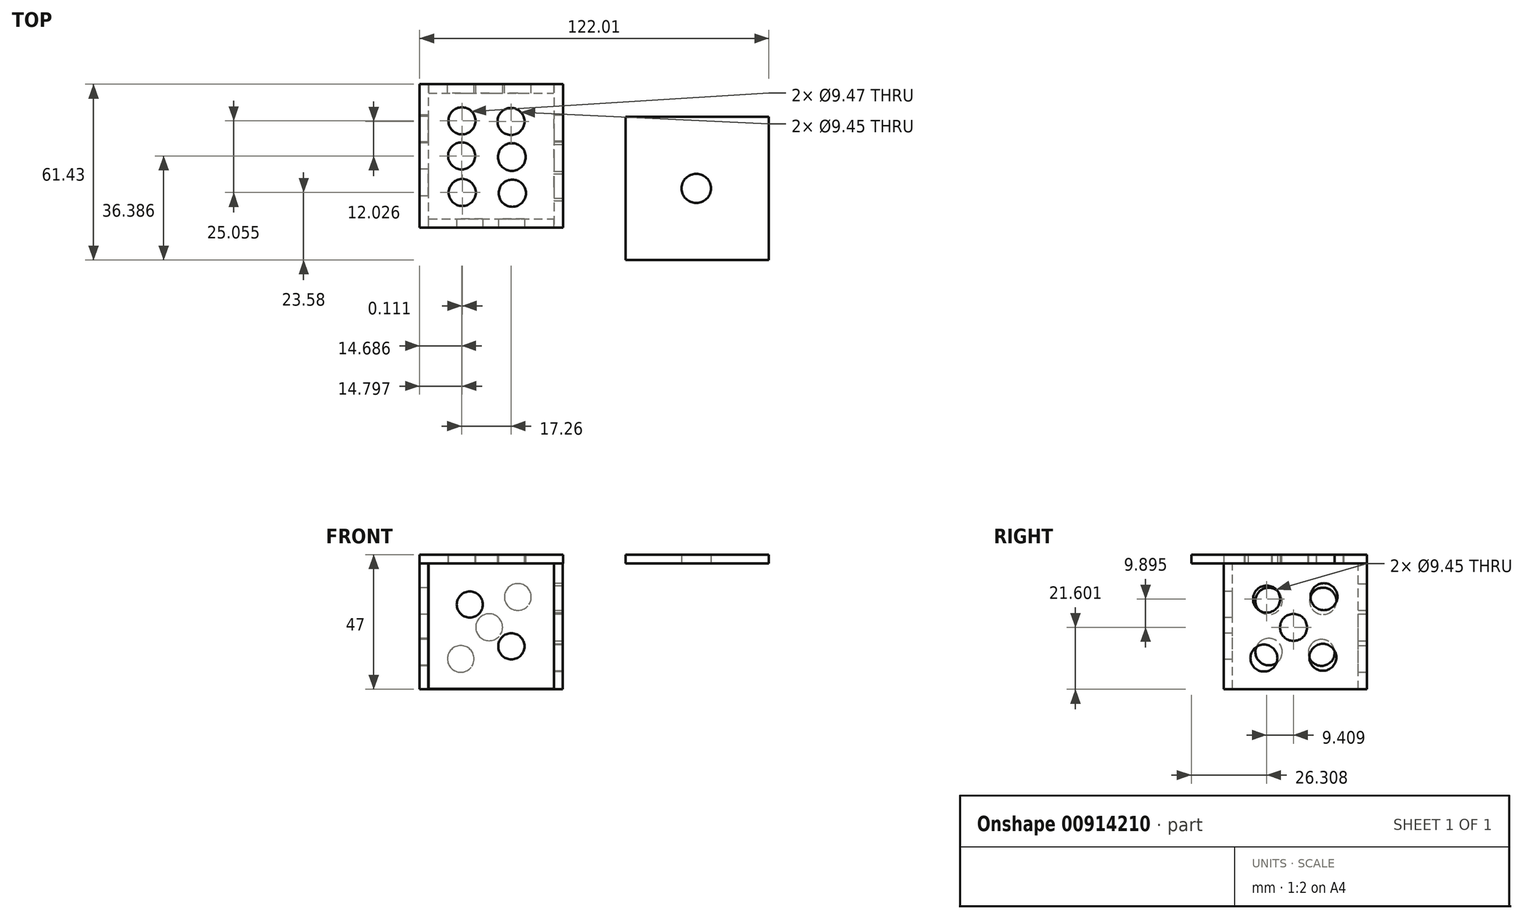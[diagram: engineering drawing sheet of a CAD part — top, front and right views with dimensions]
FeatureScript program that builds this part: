
annotation { "Feature Type Name" : "Feature", "Feature Type Description" : "" }
export const myFeature = defineFeature(function(context is Context, id is Id, definition is map)
    precondition{}
    {
        {
            var Q0;
            Q0=qCreatedBy(makeId("Top.planeOp"),FACE);
            var sketch = newSketch(context, id + "F0", { "sketchPlane" : qUnion([Q0])});
            skLineSegment(sketch, "E0.bottom", {"start": v(-67.18, 63.94) * mm, "end": v(-17.07, 63.94) * mm});
            skLineSegment(sketch, "E0.top", {"start": v(-67.18, 13.83) * mm, "end": v(-17.07, 13.83) * mm});
            skLineSegment(sketch, "E0.left", {"start": v(-67.18, 63.94) * mm, "end": v(-67.18, 13.83) * mm});
            skLineSegment(sketch, "E0.right", {"start": v(-17.07, 63.94) * mm, "end": v(-17.07, 13.83) * mm});
            skSolve(sketch);
        }
        {
            var Q0;
            Q0 = qSketchRegion(id + "F0", true);
            extrude(context, id + "F1", {"entities" : qUnion([Q0]), "depth" : 3 * mm, "offsetDistance" : 25 * mm});
        }
        {
            var Q0;
            Q0=qCreatedBy(makeId("Top.planeOp"),FACE);
            var sketch = newSketch(context, id + "F2", { "sketchPlane" : qUnion([Q0])});
            skLineSegment(sketch, "E1.bottom", {"start": v(-17.24, 63.94) * mm, "end": v(-20.28, 63.94) * mm});
            skLineSegment(sketch, "E1.top", {"start": v(-17.24, 13.82) * mm, "end": v(-20.28, 13.82) * mm});
            skLineSegment(sketch, "E1.left", {"start": v(-17.24, 63.94) * mm, "end": v(-17.24, 13.82) * mm});
            skLineSegment(sketch, "E1.right", {"start": v(-20.28, 63.94) * mm, "end": v(-20.28, 13.82) * mm});
            skSolve(sketch);
        }
        {
            var Q0;
            Q0 = qSketchRegion(id + "F2", true);
            extrude(context, id + "F3", {"entities" : qUnion([Q0]), "operationType" : NewBodyOperationType.ADD, "oppositeDirection" : true, "depth" : 44 * mm, "offsetDistance" : 25 * mm});
        }
        {
            var Q0;
            Q0=qCreatedBy(makeId("Top.planeOp"),FACE);
            var sketch = newSketch(context, id + "F4", { "sketchPlane" : qUnion([Q0])});
            skLineSegment(sketch, "E2.bottom", {"start": v(-67.2, 63.94) * mm, "end": v(-64.15, 63.94) * mm});
            skLineSegment(sketch, "E2.top", {"start": v(-67.2, 13.89) * mm, "end": v(-64.15, 13.89) * mm});
            skLineSegment(sketch, "E2.left", {"start": v(-67.2, 63.94) * mm, "end": v(-67.2, 13.89) * mm});
            skLineSegment(sketch, "E2.right", {"start": v(-64.15, 63.94) * mm, "end": v(-64.15, 13.89) * mm});
            skSolve(sketch);
        }
        {
            var Q0;
            Q0 = qSketchRegion(id + "F4", true);
            extrude(context, id + "F5", {"entities" : qUnion([Q0]), "operationType" : NewBodyOperationType.ADD, "oppositeDirection" : true, "depth" : 44 * mm, "offsetDistance" : 25 * mm});
        }
        {
            var Q0;
            Q0=qCreatedBy(makeId("Top.planeOp"),FACE);
            var sketch = newSketch(context, id + "F6", { "sketchPlane" : qUnion([Q0])});
            skLineSegment(sketch, "E3.bottom", {"start": v(-64.05, 13.88) * mm, "end": v(-20.01, 13.88) * mm});
            skLineSegment(sketch, "E3.top", {"start": v(-64.05, 16.88) * mm, "end": v(-20.01, 16.88) * mm});
            skLineSegment(sketch, "E3.left", {"start": v(-64.05, 13.88) * mm, "end": v(-64.05, 16.88) * mm});
            skLineSegment(sketch, "E3.right", {"start": v(-20.01, 13.88) * mm, "end": v(-20.01, 16.88) * mm});
            skSolve(sketch);
        }
        {
            var Q0;
            Q0 = qSketchRegion(id + "F6", true);
            extrude(context, id + "F7", {"entities" : qUnion([Q0]), "operationType" : NewBodyOperationType.ADD, "oppositeDirection" : true, "depth" : 43.8 * mm, "offsetDistance" : 25 * mm});
        }
        {
            var Q0;
            Q0=qCreatedBy(makeId("Top.planeOp"),FACE);
            var sketch = newSketch(context, id + "F8", { "sketchPlane" : qUnion([Q0])});
            skLineSegment(sketch, "E4.bottom", {"start": v(-64.1, 63.88) * mm, "end": v(-20.32, 63.88) * mm});
            skLineSegment(sketch, "E4.top", {"start": v(-64.1, 60.83) * mm, "end": v(-20.32, 60.83) * mm});
            skLineSegment(sketch, "E4.left", {"start": v(-64.1, 63.88) * mm, "end": v(-64.1, 60.83) * mm});
            skLineSegment(sketch, "E4.right", {"start": v(-20.32, 63.88) * mm, "end": v(-20.32, 60.83) * mm});
            skSolve(sketch);
        }
        {
            var Q0;
            Q0 = qSketchRegion(id + "F8", true);
            extrude(context, id + "F9", {"entities" : qUnion([Q0]), "operationType" : NewBodyOperationType.ADD, "oppositeDirection" : true, "depth" : 44 * mm, "offsetDistance" : 25 * mm});
        }
        {
            var Q0;
            Q0=qCreatedBy(makeId("Top.planeOp"),FACE);
            var sketch = newSketch(context, id + "F10", { "sketchPlane" : qUnion([Q0])});
            skLineSegment(sketch, "E5.bottom", {"start": v(4.73, 2.51) * mm, "end": v(54.81, 2.51) * mm});
            skLineSegment(sketch, "E5.top", {"start": v(4.73, 52.6) * mm, "end": v(54.81, 52.6) * mm});
            skLineSegment(sketch, "E5.left", {"start": v(4.73, 2.51) * mm, "end": v(4.73, 52.6) * mm});
            skLineSegment(sketch, "E5.right", {"start": v(54.81, 2.51) * mm, "end": v(54.81, 52.6) * mm});
            skSolve(sketch);
        }
        {
            var Q0;
            Q0 = qSketchRegion(id + "F10", true);
            extrude(context, id + "F11", {"entities" : qUnion([Q0]), "depth" : 3 * mm, "offsetDistance" : 25 * mm});
        }
        {
            var Q0;
            Q0=makeQuery(id+"F11.opExtrude","CAP_FACE",FACE,{"disambiguationData":[OSD([sQuery(id+"F10.wireOp",EDGE,"E5.bottom"),sQuery(id+"F10.wireOp",EDGE,"E5.top"),sQuery(id+"F10.wireOp",EDGE,"E5.left"),sQuery(id+"F10.wireOp",EDGE,"E5.right")])],"isStart":true});
            var sketch = newSketch(context, id + "F12", { "sketchPlane" : qUnion([Q0])});
            skCircle(sketch, "E6", {"center": v(29.5, -27.53) * mm, "radius": 5.12 * mm});
            skSolve(sketch);
        }
        {
            var Q0;
            Q0=makeQuery(id+"F12.imprint","IMPRINT",FACE,{"disambiguationData":[TD([[makeQuery(id+"F12.imprint","IMPRINT",EDGE,{"derivedFrom":sQuery(id+"F12.wireOp",EDGE,"E6")}),1.0]])]});
            var Q1;
            Q1=sQuery(id+"F12.wireOp",EDGE,"E6");
            extrude(context, id + "F13", {"entities" : qUnion([Q0]), "operationType" : NewBodyOperationType.REMOVE, "surfaceEntities" : qUnion([Q1]), "oppositeDirection" : true, "depth" : 26 * mm, "offsetDistance" : 25 * mm});
        }
        {
            var Q0;
            Q0=qCreatedBy(makeId("Front.planeOp"),FACE);
            var sketch = newSketch(context, id + "F14", { "sketchPlane" : qUnion([Q0])});
            skCircle(sketch, "E7", {"center": v(-49.65, -14.4) * mm, "radius": 4.55 * mm});
            skCircle(sketch, "E8", {"center": v(-35.14, -29) * mm, "radius": 4.58 * mm});
            skSolve(sketch);
        }
        {
            var Q0;
            Q0 = qSketchRegion(id + "F14", true);
            extrude(context, id + "F15", {"entities" : qUnion([Q0]), "operationType" : NewBodyOperationType.REMOVE, "oppositeDirection" : true, "depth" : 35.9 * mm, "offsetDistance" : 25 * mm});
        }
        {
            var Q0;
            Q0=makeQuery(id+"F9.opExtrude","SWEPT_FACE",FACE,{"disambiguationData":[OSD([sQuery(id+"F8.wireOp",EDGE,"E4.bottom")])]});
            var sketch = newSketch(context, id + "F16", { "sketchPlane" : qUnion([Q0])});
            skCircle(sketch, "E9", {"center": v(52.81, -33.4) * mm, "radius": 4.65 * mm});
            skCircle(sketch, "E10", {"center": v(42.89, -22.35) * mm, "radius": 4.7 * mm});
            skCircle(sketch, "E11", {"center": v(32.87, -11.77) * mm, "radius": 4.68 * mm});
            skSolve(sketch);
        }
        {
            var Q0;
            Q0=makeQuery(id+"F16.imprint","IMPRINT",FACE,{"disambiguationData":[TD([[makeQuery(id+"F16.imprint","IMPRINT",EDGE,{"derivedFrom":sQuery(id+"F16.wireOp",EDGE,"E11")}),1.0]])]});
            var Q1;
            Q1=makeQuery(id+"F16.imprint","IMPRINT",FACE,{"disambiguationData":[TD([[makeQuery(id+"F16.imprint","IMPRINT",EDGE,{"derivedFrom":sQuery(id+"F16.wireOp",EDGE,"E9")}),1.0]])]});
            var Q2;
            Q2=makeQuery(id+"F16.imprint","IMPRINT",FACE,{"disambiguationData":[TD([[makeQuery(id+"F16.imprint","IMPRINT",EDGE,{"derivedFrom":sQuery(id+"F16.wireOp",EDGE,"E10")}),1.0]])]});
            extrude(context, id + "F17", {"entities" : qUnion([Q0, Q1, Q2]), "operationType" : NewBodyOperationType.REMOVE, "oppositeDirection" : true, "depth" : 17.8 * mm, "offsetDistance" : 25 * mm});
        }
        {
            var Q0;
            Q0=makeQuery(id+"F5.opExtrude","SWEPT_FACE",FACE,{"disambiguationData":[OSD([sQuery(id+"F4.wireOp",EDGE,"E2.left")])]});
            var sketch = newSketch(context, id + "F18", { "sketchPlane" : qUnion([Q0])});
            skCircle(sketch, "E12", {"center": v(-48, -31.2) * mm, "radius": 4.62 * mm});
            skCircle(sketch, "E13", {"center": v(-29.6, -13.2) * mm, "radius": 4.68 * mm});
            skCircle(sketch, "E14", {"center": v(-29.6, -30.94) * mm, "radius": 4.7 * mm});
            skCircle(sketch, "E15", {"center": v(-48.53, -13.2) * mm, "radius": 4.68 * mm});
            skSolve(sketch);
        }
        {
            var Q0;
            Q0=makeQuery(id+"F18.imprint","IMPRINT",FACE,{"disambiguationData":[TD([[makeQuery(id+"F18.imprint","IMPRINT",EDGE,{"derivedFrom":sQuery(id+"F18.wireOp",EDGE,"E15")}),1.0]])]});
            var Q1;
            Q1=makeQuery(id+"F18.imprint","IMPRINT",FACE,{"disambiguationData":[TD([[makeQuery(id+"F18.imprint","IMPRINT",EDGE,{"derivedFrom":sQuery(id+"F18.wireOp",EDGE,"E14")}),1.0]])]});
            var Q2;
            Q2=makeQuery(id+"F18.imprint","IMPRINT",FACE,{"disambiguationData":[TD([[makeQuery(id+"F18.imprint","IMPRINT",EDGE,{"derivedFrom":sQuery(id+"F18.wireOp",EDGE,"E12")}),1.0]])]});
            var Q3;
            Q3=makeQuery(id+"F18.imprint","IMPRINT",FACE,{"disambiguationData":[TD([[makeQuery(id+"F18.imprint","IMPRINT",EDGE,{"derivedFrom":sQuery(id+"F18.wireOp",EDGE,"E13")}),1.0]])]});
            extrude(context, id + "F19", {"entities" : qUnion([Q0, Q1, Q2, Q3]), "operationType" : NewBodyOperationType.REMOVE, "oppositeDirection" : true, "depth" : 22.9 * mm, "offsetDistance" : 25 * mm});
        }
        {
            var Q0;
            Q0=makeQuery(id+"F1.opExtrude","CAP_FACE",FACE,{"disambiguationData":[OSD([sQuery(id+"F0.wireOp",EDGE,"E0.bottom"),sQuery(id+"F0.wireOp",EDGE,"E0.top"),sQuery(id+"F0.wireOp",EDGE,"E0.left"),sQuery(id+"F0.wireOp",EDGE,"E0.right")])],"isStart":false});
            var sketch = newSketch(context, id + "F20", { "sketchPlane" : qUnion([Q0])});
            skCircle(sketch, "E16", {"center": v(-52.4, 51.14) * mm, "radius": 4.73 * mm});
            skCircle(sketch, "E17", {"center": v(-35.25, 50.92) * mm, "radius": 4.72 * mm});
            skCircle(sketch, "E18", {"center": v(-52.51, 38.9) * mm, "radius": 4.73 * mm});
            skCircle(sketch, "E19", {"center": v(-34.96, 38.5) * mm, "radius": 4.84 * mm});
            skCircle(sketch, "E20", {"center": v(-52.3, 26.09) * mm, "radius": 4.73 * mm});
            skCircle(sketch, "E21", {"center": v(-34.79, 25.85) * mm, "radius": 4.76 * mm});
            skSolve(sketch);
        }
        {
            var Q0;
            Q0 = qSketchRegion(id + "F20", true);
            extrude(context, id + "F21", {"entities" : qUnion([Q0]), "operationType" : NewBodyOperationType.REMOVE, "oppositeDirection" : true, "depth" : 47.9 * mm, "offsetDistance" : 25 * mm});
        }
        {
            var Q0;
            Q0=makeQuery(id+"F3.opExtrude","SWEPT_FACE",FACE,{"disambiguationData":[OSD([sQuery(id+"F2.wireOp",EDGE,"E1.left")])]});
            var sketch = newSketch(context, id + "F22", { "sketchPlane" : qUnion([Q0])});
            skCircle(sketch, "E22", {"center": v(27.88, -33.1) * mm, "radius": 4.71 * mm});
            skCircle(sketch, "E23", {"center": v(28.82, -12.5) * mm, "radius": 4.73 * mm});
            skCircle(sketch, "E24", {"center": v(48.48, -32.85) * mm, "radius": 4.7 * mm});
            skCircle(sketch, "E25", {"center": v(48.86, -11.66) * mm, "radius": 4.7 * mm});
            skCircle(sketch, "E26", {"center": v(38.23, -22.4) * mm, "radius": 4.72 * mm});
            skSolve(sketch);
        }
        {
            var Q0;
            Q0 = qSketchRegion(id + "F22", true);
            extrude(context, id + "F23", {"entities" : qUnion([Q0]), "operationType" : NewBodyOperationType.REMOVE, "oppositeDirection" : true, "depth" : 10.5 * mm, "offsetDistance" : 25 * mm});
        }
    });
